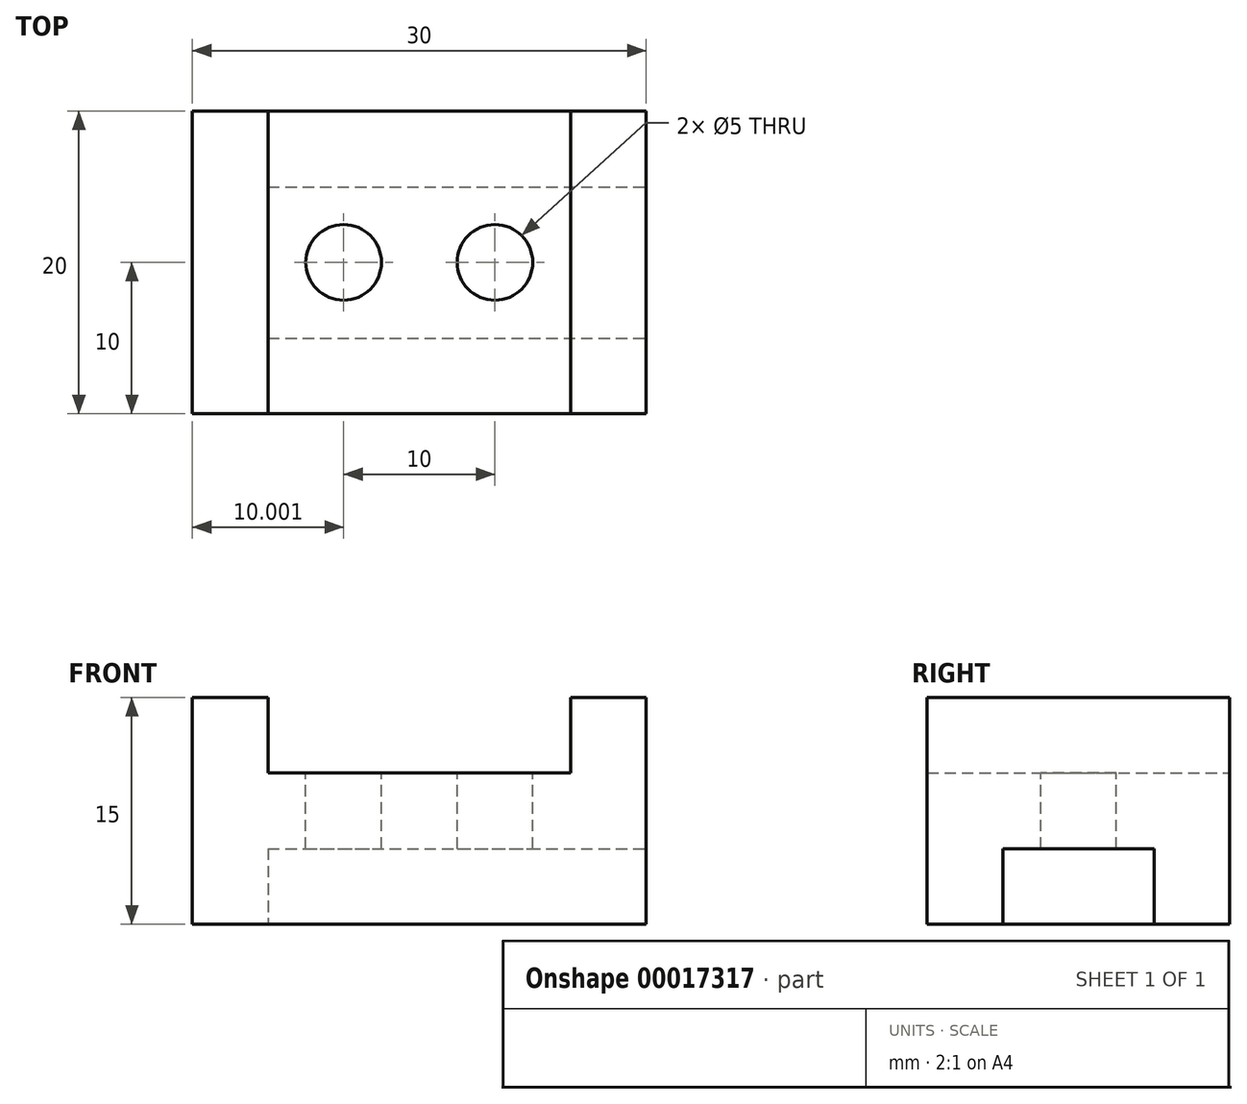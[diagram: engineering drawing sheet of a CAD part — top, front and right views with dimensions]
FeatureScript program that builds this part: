
annotation { "Feature Type Name" : "Feature", "Feature Type Description" : "" }
export const myFeature = defineFeature(function(context is Context, id is Id, definition is map)
    precondition{}
    {
        {
            var Q0;
            Q0=qCreatedBy(makeId("Front.planeOp"),FACE);
            var sketch = newSketch(context, id + "F0", { "sketchPlane" : qUnion([Q0])});
            skLineSegment(sketch, "E0", {"start": v(-17.26, 6.25) * mm, "end": v(-12.26, 6.25) * mm});
            skLineSegment(sketch, "E1", {"start": v(-12.26, 6.25) * mm, "end": v(-12.26, 1.25) * mm});
            skLineSegment(sketch, "E2", {"start": v(-12.26, 1.25) * mm, "end": v(7.74, 1.25) * mm});
            skLineSegment(sketch, "E3", {"start": v(7.74, 1.25) * mm, "end": v(7.74, 6.25) * mm});
            skLineSegment(sketch, "E4", {"start": v(7.74, 6.25) * mm, "end": v(12.74, 6.25) * mm});
            skLineSegment(sketch, "E5", {"start": v(12.74, 6.25) * mm, "end": v(12.74, -8.75) * mm});
            skLineSegment(sketch, "E6", {"start": v(12.74, -8.75) * mm, "end": v(-17.26, -8.75) * mm});
            skLineSegment(sketch, "E7", {"start": v(-17.26, -8.75) * mm, "end": v(-17.26, 6.25) * mm});
            skSolve(sketch);
        }
        {
            var Q0;
            Q0=makeQuery(id+"F0.imprint","IMPRINT",FACE,{"disambiguationData":[TD([[makeQuery(id+"F0.imprint","IMPRINT",EDGE,{"derivedFrom":sQuery(id+"F0.wireOp",EDGE,"E0")}),-1.0]])]});
            extrude(context, id + "F1", {"entities" : qUnion([Q0]), "depth" : 20 * mm});
        }
        {
            var Q0;
            Q0=makeQuery(id+"F1.opExtrude","SWEPT_FACE",FACE,{"disambiguationData":[OSD([sQuery(id+"F0.wireOp",EDGE,"E5")])]});
            var sketch = newSketch(context, id + "F2", { "sketchPlane" : qUnion([Q0])});
            skLineSegment(sketch, "E8", {"start": v(-15, -3.75) * mm, "end": v(-5, -3.75) * mm});
            skLineSegment(sketch, "E9", {"start": v(-5, -3.75) * mm, "end": v(-5, -8.75) * mm});
            skLineSegment(sketch, "E10", {"start": v(-15, -3.75) * mm, "end": v(-15, -8.75) * mm});
            skSolve(sketch);
        }
        {
            var Q0;
            Q0=makeQuery(id+"F2.imprint","IMPRINT",FACE,{"disambiguationData":[TD([[makeQuery(id+"F2.imprint","IMPRINT",EDGE,{"derivedFrom":sQuery(id+"F2.wireOp",EDGE,"E8")}),-1.0]])]});
            extrude(context, id + "F3", {"entities" : qUnion([Q0]), "operationType" : NewBodyOperationType.REMOVE, "oppositeDirection" : true, "depth" : 25 * mm});
        }
        {
            var Q0;
            Q0=makeQuery(id+"F1.opExtrude","SWEPT_FACE",FACE,{"disambiguationData":[OSD([sQuery(id+"F0.wireOp",EDGE,"E2")])]});
            var sketch = newSketch(context, id + "F4", { "sketchPlane" : qUnion([Q0])});
            skCircle(sketch, "E11", {"center": v(-7.26, -10) * mm, "radius": 2.5 * mm});
            skCircle(sketch, "E12", {"center": v(2.74, -10) * mm, "radius": 2.5 * mm});
            skSolve(sketch);
        }
        {
            var Q0;
            Q0=makeQuery(id+"F4.imprint","IMPRINT",FACE,{"disambiguationData":[TD([[makeQuery(id+"F4.imprint","IMPRINT",EDGE,{"derivedFrom":sQuery(id+"F4.wireOp",EDGE,"E11")}),1.0]])]});
            var Q1;
            Q1=makeQuery(id+"F4.imprint","IMPRINT",FACE,{"disambiguationData":[TD([[makeQuery(id+"F4.imprint","IMPRINT",EDGE,{"derivedFrom":sQuery(id+"F4.wireOp",EDGE,"E12")}),1.0]])]});
            extrude(context, id + "F5", {"entities" : qUnion([Q0, Q1]), "operationType" : NewBodyOperationType.REMOVE, "oppositeDirection" : true, "depth" : 25 * mm});
        }
    });
